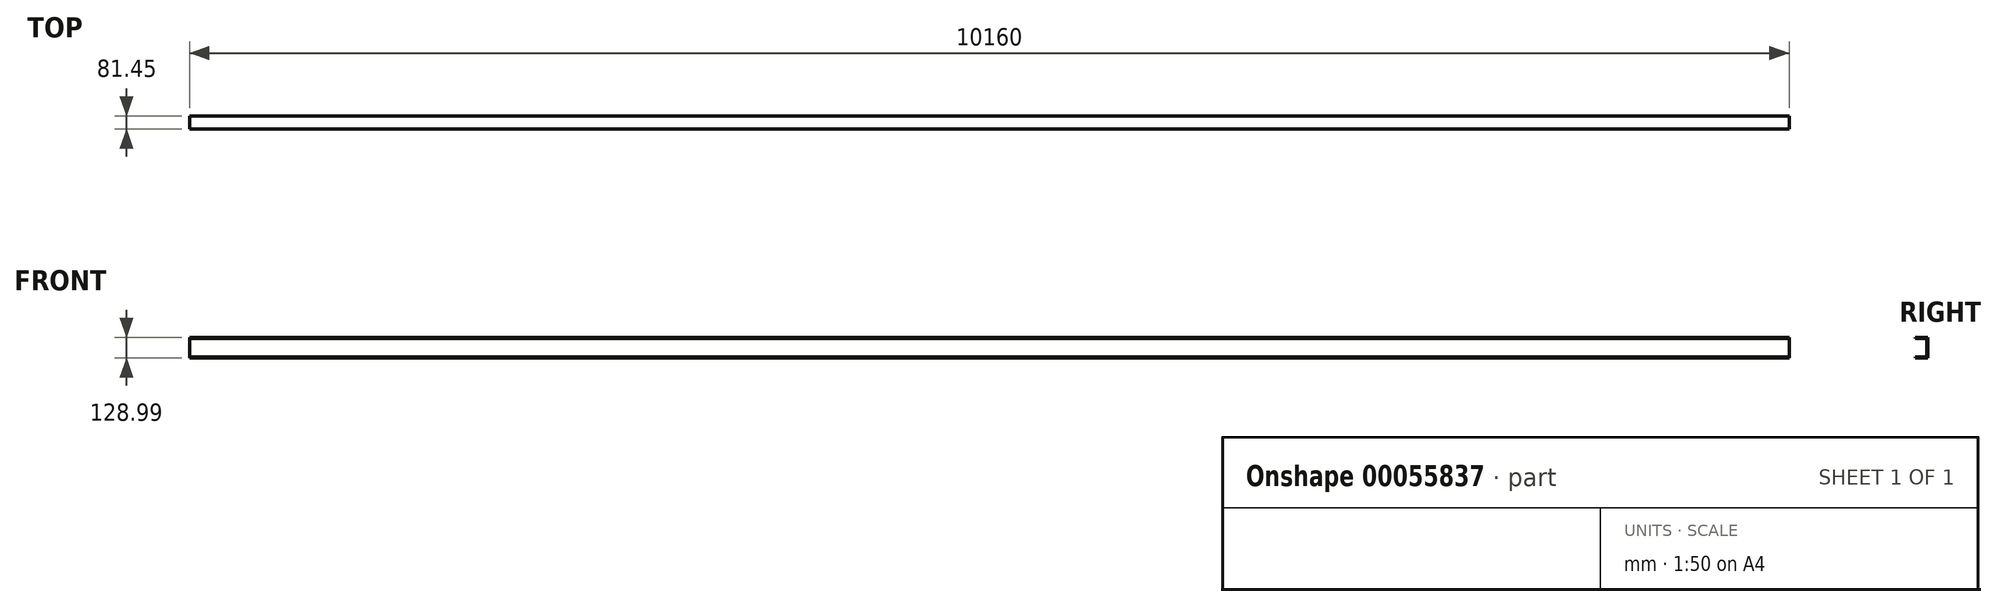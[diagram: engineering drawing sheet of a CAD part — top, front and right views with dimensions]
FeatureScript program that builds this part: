
annotation { "Feature Type Name" : "Feature", "Feature Type Description" : "" }
export const myFeature = defineFeature(function(context is Context, id is Id, definition is map)
    precondition{}
    {
        {
            var Q0;
            Q0=qCreatedBy(makeId("Right.planeOp"),FACE);
            var sketch = newSketch(context, id + "F0", { "sketchPlane" : qUnion([Q0])});
            skLineSegment(sketch, "E0", {"start": v(-102.62, 60.3) * mm, "end": v(-21.17, 60.3) * mm});
            skLineSegment(sketch, "E1", {"start": v(-21.17, 60.3) * mm, "end": v(-21.17, -68.7) * mm});
            skLineSegment(sketch, "E2", {"start": v(-21.17, -68.7) * mm, "end": v(-102.62, -68.7) * mm});
            skLineSegment(sketch, "E3.0", {"start": v(-27.52, -62.35) * mm, "end": v(-102.62, -62.35) * mm});
            skLineSegment(sketch, "E3.1", {"start": v(-27.52, 53.94) * mm, "end": v(-27.52, -62.35) * mm});
            skLineSegment(sketch, "E3.2", {"start": v(-102.62, 53.94) * mm, "end": v(-27.52, 53.94) * mm});
            skLineSegment(sketch, "E4", {"start": v(-102.62, 60.3) * mm, "end": v(-102.62, 53.94) * mm});
            skLineSegment(sketch, "E5", {"start": v(-102.62, -62.35) * mm, "end": v(-102.62, -68.7) * mm});
            skSolve(sketch);
        }
        {
            var Q0;
            Q0=makeQuery(id+"F0.imprint","IMPRINT",FACE,{"disambiguationData":[TD([[makeQuery(id+"F0.imprint","IMPRINT",EDGE,{"derivedFrom":sQuery(id+"F0.wireOp",EDGE,"E0")}),-1.0]])]});
            extrude(context, id + "F1", {"entities" : qUnion([Q0]), "endBound" : BoundingType.SYMMETRIC, "depth" : 10160 * mm});
        }
    });
